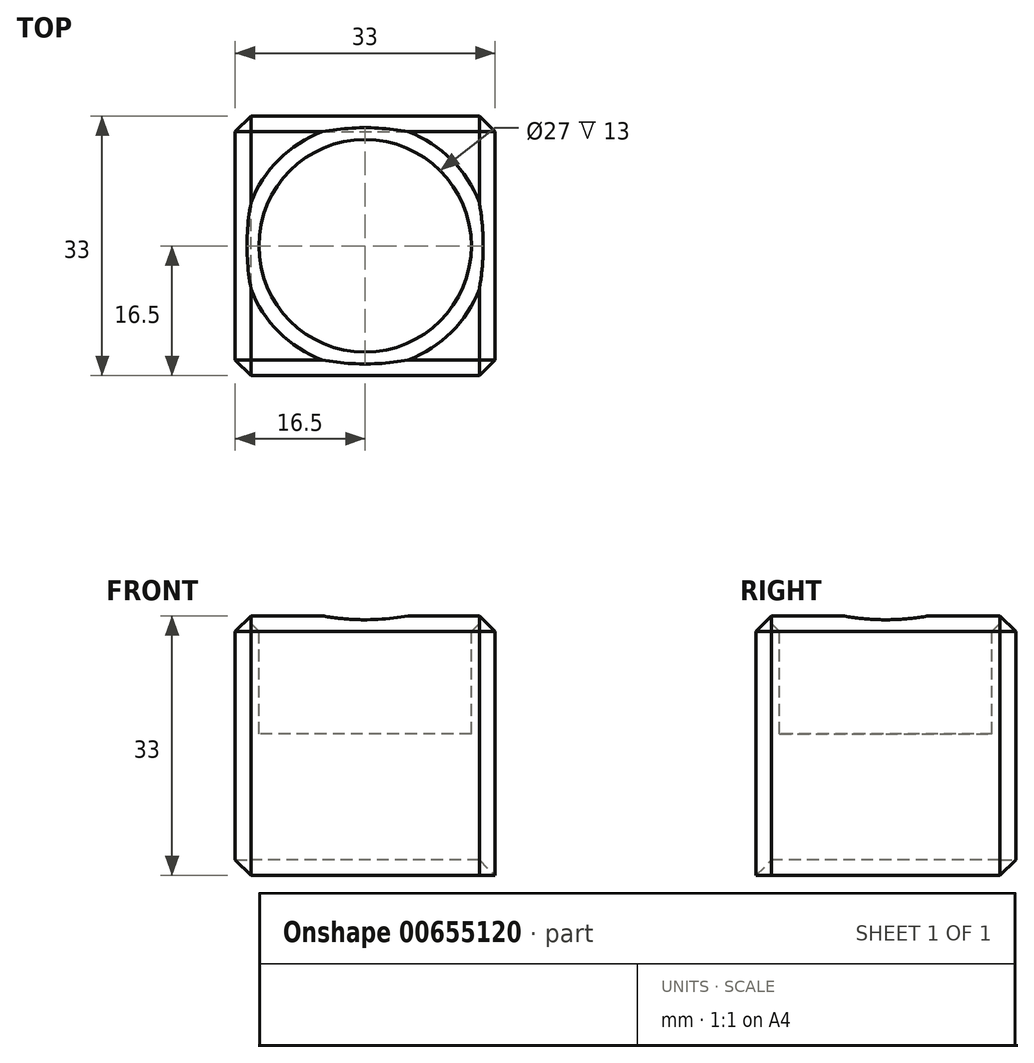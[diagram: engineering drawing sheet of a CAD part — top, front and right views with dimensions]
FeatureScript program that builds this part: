
annotation { "Feature Type Name" : "Feature", "Feature Type Description" : "" }
export const myFeature = defineFeature(function(context is Context, id is Id, definition is map)
    precondition{}
    {
        {
            var Q0;
            Q0=qCreatedBy(makeId("Front.planeOp"),FACE);
            var sketch = newSketch(context, id + "F0", { "sketchPlane" : qUnion([Q0])});
            skLineSegment(sketch, "E0.bottom", {"start": v(-16.5, 0) * mm, "end": v(16.5, 0) * mm});
            skLineSegment(sketch, "E0.top", {"start": v(-16.5, 33) * mm, "end": v(16.5, 33) * mm});
            skLineSegment(sketch, "E0.left", {"start": v(-16.5, 0) * mm, "end": v(-16.5, 33) * mm});
            skLineSegment(sketch, "E0.right", {"start": v(16.5, 0) * mm, "end": v(16.5, 33) * mm});
            skSolve(sketch);
        }
        {
            var Q0;
            Q0=qSketchRegion(id+"F0",true);
            extrude(context, id + "F1", {"entities" : qUnion([Q0]), "depth" : 33 * mm, "offsetDistance" : 25 * mm, "symmetric" : true});
        }
        {
            var Q0;
            Q0=makeQuery(id+"F1.opExtrude","SWEPT_FACE",FACE,{"disambiguationData":[OSD([sQuery(id+"F0.wireOp",EDGE,"E0.top")])]});
            var sketch = newSketch(context, id + "F2", { "sketchPlane" : qUnion([Q0])});
            skCircle(sketch, "E1", {"center": v(0, 0) * mm, "radius": 13.5 * mm});
            skSolve(sketch);
        }
        {
            var Q0;
            Q0=makeQuery(id+"F2.imprint","IMPRINT",FACE,{"disambiguationData":[TD([[makeQuery(id+"F2.imprint","IMPRINT",EDGE,{"derivedFrom":sQuery(id+"F2.wireOp",EDGE,"E1")}),1.0]])]});
            extrude(context, id + "F3", {"entities" : qUnion([Q0]), "operationType" : NewBodyOperationType.REMOVE, "oppositeDirection" : true, "depth" : 15 * mm, "offsetDistance" : 25 * mm});
        }
        {
            var Q0;
            Q0=makeQuery(id+"F1.opExtrude","SWEPT_FACE",FACE,{"disambiguationData":[OSD([sQuery(id+"F0.wireOp",EDGE,"E0.top")])]});
            var Q1;
            Q1=makeQuery(id+"F1.opExtrude","CAP_FACE",FACE,{"disambiguationData":[OSD([sQuery(id+"F0.wireOp",EDGE,"E0.bottom"),sQuery(id+"F0.wireOp",EDGE,"E0.top"),sQuery(id+"F0.wireOp",EDGE,"E0.left"),sQuery(id+"F0.wireOp",EDGE,"E0.right")])],"isStart":true});
            var Q2;
            Q2=makeQuery(id+"F1.opExtrude","SWEPT_FACE",FACE,{"disambiguationData":[OSD([sQuery(id+"F0.wireOp",EDGE,"E0.left")])]});
            var Q3;
            Q3=makeQuery(id+"F1.opExtrude","CAP_EDGE",EDGE,{"disambiguationData":[OSD([sQuery(id+"F0.wireOp",EDGE,"E0.right")])],"isStart":false});
            var Q4;
            Q4=makeQuery(id+"FdIHFxNJdluCD95_1.opExtrude","CAP_FACE",FACE,{"disambiguationData":[OSD([sQuery(id+"Fu96pWnszwZyr60_1.wireOp",EDGE,"IQmaCKBv-J2y3-nUDz-vwEx-fTrJKZ2k2HmQ"),sQuery(id+"Fu96pWnszwZyr60_1.wireOp",EDGE,"AR93OQ27-mmQS-QI7t-DQ6d-JprsfBQbTBwf"),sQuery(id+"Fu96pWnszwZyr60_1.wireOp",EDGE,"601d5cff-1262-40f4-b0c4-98792585f77f.1.0"),sQuery(id+"Fu96pWnszwZyr60_1.wireOp",EDGE,"601d5cff-1262-40f4-b0c4-98792585f77f.2.0"),sQuery(id+"Fu96pWnszwZyr60_1.wireOp",EDGE,"82cedc39-13b2-4569-92ae-15cde86b9581.1.3.0"),sQuery(id+"Fu96pWnszwZyr60_1.wireOp",EDGE,"012d5c37-e0d3-4e87-9748-09dcf38a7d3d.trimOffspring"),sQuery(id+"Fu96pWnszwZyr60_1.wireOp",EDGE,"9fdec678-acab-4987-a636-344b30e0dadb.trimOffspring"),sQuery(id+"Fu96pWnszwZyr60_1.wireOp",EDGE,"fb67608c-e535-4871-b19e-7fdc38bc7386.trimOffspring")])],"isStart":false});
            var Q5;
            Q5=makeQuery(id+"FjXE2MBLlm6NdZQ_1.opExtrude","CAP_FACE",FACE,{"disambiguationData":[OSD([sQuery(id+"FHS1gO03yPvXPNt_1.wireOp",EDGE,"bc334e88-59e3-408d-b6d8-33b89ba461c3"),sQuery(id+"FHS1gO03yPvXPNt_1.wireOp",EDGE,"G3EWnRT5-Nfps-zY3r-q0pE-yUGAUCAEDP1n"),sQuery(id+"FHS1gO03yPvXPNt_1.wireOp",EDGE,"62aa8f99-3a60-4bd1-ad04-aae5d2ee14aa.1.0"),sQuery(id+"FHS1gO03yPvXPNt_1.wireOp",EDGE,"62aa8f99-3a60-4bd1-ad04-aae5d2ee14aa.2.0"),sQuery(id+"FHS1gO03yPvXPNt_1.wireOp",EDGE,"62aa8f99-3a60-4bd1-ad04-aae5d2ee14aa.3.0"),sQuery(id+"FHS1gO03yPvXPNt_1.wireOp",EDGE,"82ec294c-61a5-4316-ac96-efbfdecd90ef.trimOffspring"),sQuery(id+"FHS1gO03yPvXPNt_1.wireOp",EDGE,"3ee09c82-01c5-44ec-9fbe-ba587264ce73.trimOffspring"),sQuery(id+"FHS1gO03yPvXPNt_1.wireOp",EDGE,"5b752b9d-35d9-4455-a932-e743e7094a37.trimOffspring")])],"isStart":false});
            chamfer(context, id + "F4", {"entities" : qUnion([Q0, Q1, Q2, Q3, Q4, Q5]), "width" : 2 * mm, "tangentPropagation" : true});
        }
    });
